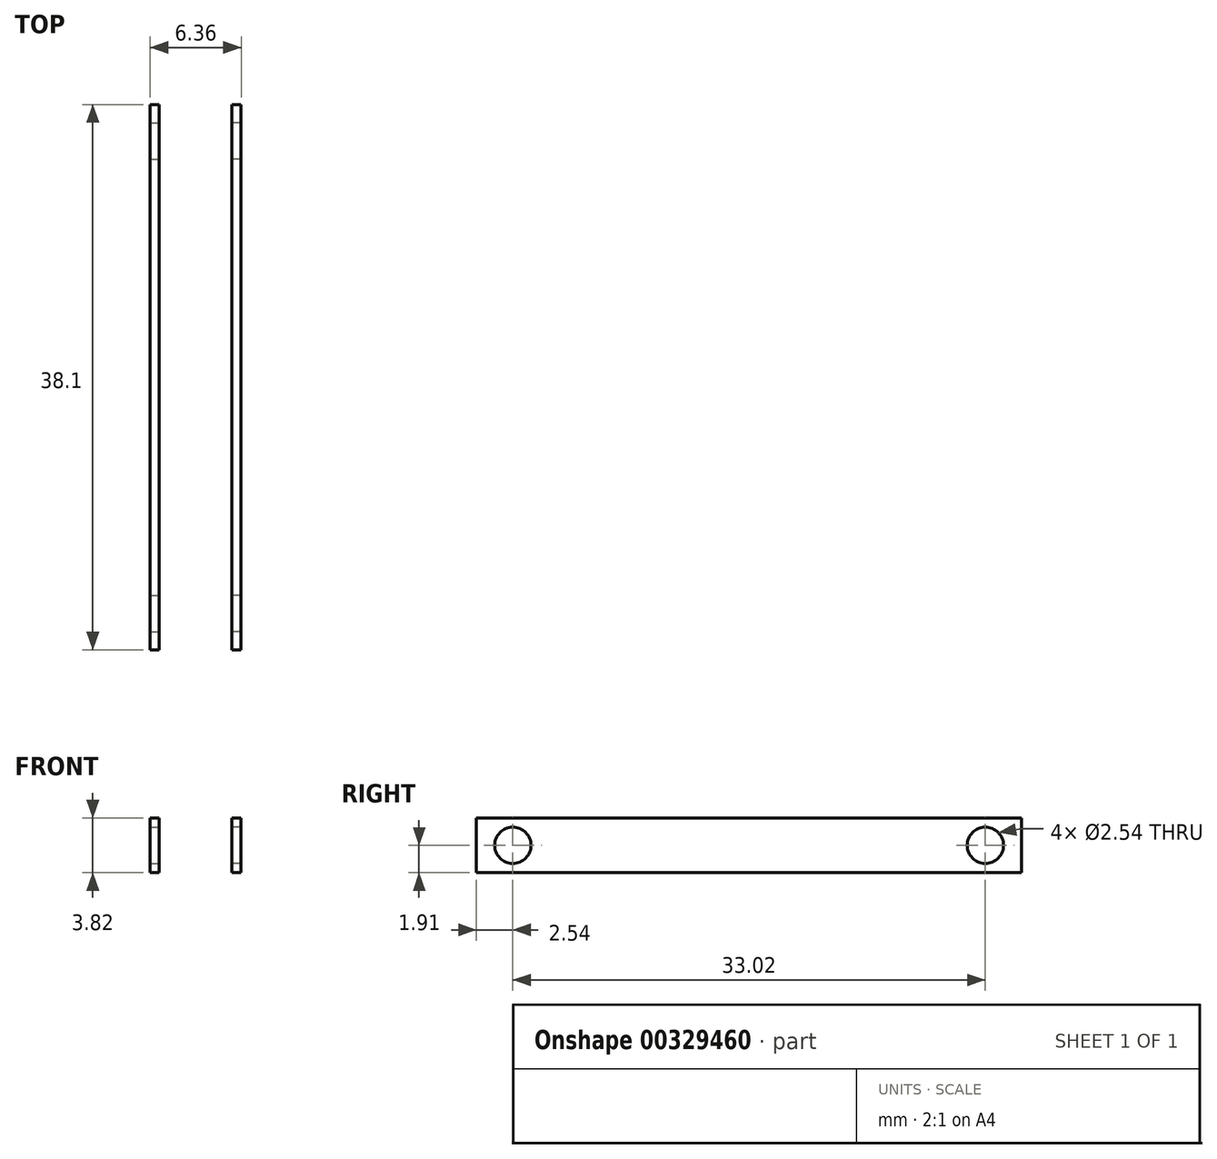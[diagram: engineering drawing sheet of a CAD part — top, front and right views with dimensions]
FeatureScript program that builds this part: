
annotation { "Feature Type Name" : "Feature", "Feature Type Description" : "" }
export const myFeature = defineFeature(function(context is Context, id is Id, definition is map)
    precondition{}
    {
        {
            var Q0;
            Q0=qCreatedBy(makeId("Front.planeOp"),FACE);
            var sketch = newSketch(context, id + "F0", { "sketchPlane" : qUnion([Q0])});
            skLineSegment(sketch, "E0.bottom", {"start": v(-3.18, 1.9) * mm, "end": v(-2.54, 1.9) * mm});
            skLineSegment(sketch, "E0.top", {"start": v(-3.17, -1.9) * mm, "end": v(-2.54, -1.9) * mm});
            skLineSegment(sketch, "E0.left", {"start": v(-2.54, 1.9) * mm, "end": v(-2.54, -1.9) * mm});
            skLineSegment(sketch, "E0.right", {"start": v(-3.18, 1.9) * mm, "end": v(-3.18, -1.9) * mm});
            skLineSegment(sketch, "E1.MirrorCS", {"start": v(3.18, 1.9) * mm, "end": v(2.54, 1.9) * mm});
            skLineSegment(sketch, "E2.MirrorCS", {"start": v(2.54, 1.9) * mm, "end": v(2.54, -1.9) * mm});
            skLineSegment(sketch, "E3.MirrorCS", {"start": v(3.18, 1.9) * mm, "end": v(3.18, -1.9) * mm});
            skLineSegment(sketch, "E4.MirrorCS", {"start": v(3.17, -1.9) * mm, "end": v(2.54, -1.9) * mm});
            skSolve(sketch);
        }
        {
            var Q0;
            Q0 = qSketchRegion(id + "F0", true);
            extrude(context, id + "F1", {"entities" : qUnion([Q0]), "oppositeDirection" : true, "depth" : 38.1 * mm});
        }
        {
            var Q0;
            Q0=makeQuery(id+"F1.opExtrude","SWEPT_FACE",FACE,{"disambiguationData":[OSD([sQuery(id+"F0.wireOp",EDGE,"E2.MirrorCS")])]});
            var sketch = newSketch(context, id + "F2", { "sketchPlane" : qUnion([Q0])});
            skCircle(sketch, "E5", {"center": v(-2.54, 0) * mm, "radius": 1.27 * mm});
            skCircle(sketch, "E6", {"center": v(-35.56, 0) * mm, "radius": 1.27 * mm});
            skSolve(sketch);
        }
        {
            var Q0;
            Q0 = qSketchRegion(id + "F2", true);
            extrude(context, id + "F3", {"entities" : qUnion([Q0]), "operationType" : NewBodyOperationType.REMOVE, "oppositeDirection" : true, "depth" : 11.68 * mm});
        }
        {
            var Q0;
            Q0=makeQuery(id+"F1.opExtrude","SWEPT_FACE",FACE,{"disambiguationData":[OSD([sQuery(id+"F0.wireOp",EDGE,"E0.left")])]});
            var sketch = newSketch(context, id + "F4", { "sketchPlane" : qUnion([Q0])});
            skCircle(sketch, "E7", {"center": v(2.54, 0) * mm, "radius": 1.27 * mm});
            skCircle(sketch, "E8", {"center": v(35.56, 0) * mm, "radius": 1.27 * mm});
            skSolve(sketch);
        }
        {
            var Q0;
            Q0 = qSketchRegion(id + "F4", true);
            extrude(context, id + "F5", {"entities" : qUnion([Q0]), "operationType" : NewBodyOperationType.REMOVE, "oppositeDirection" : true, "depth" : 25.4 * mm});
        }
    });
